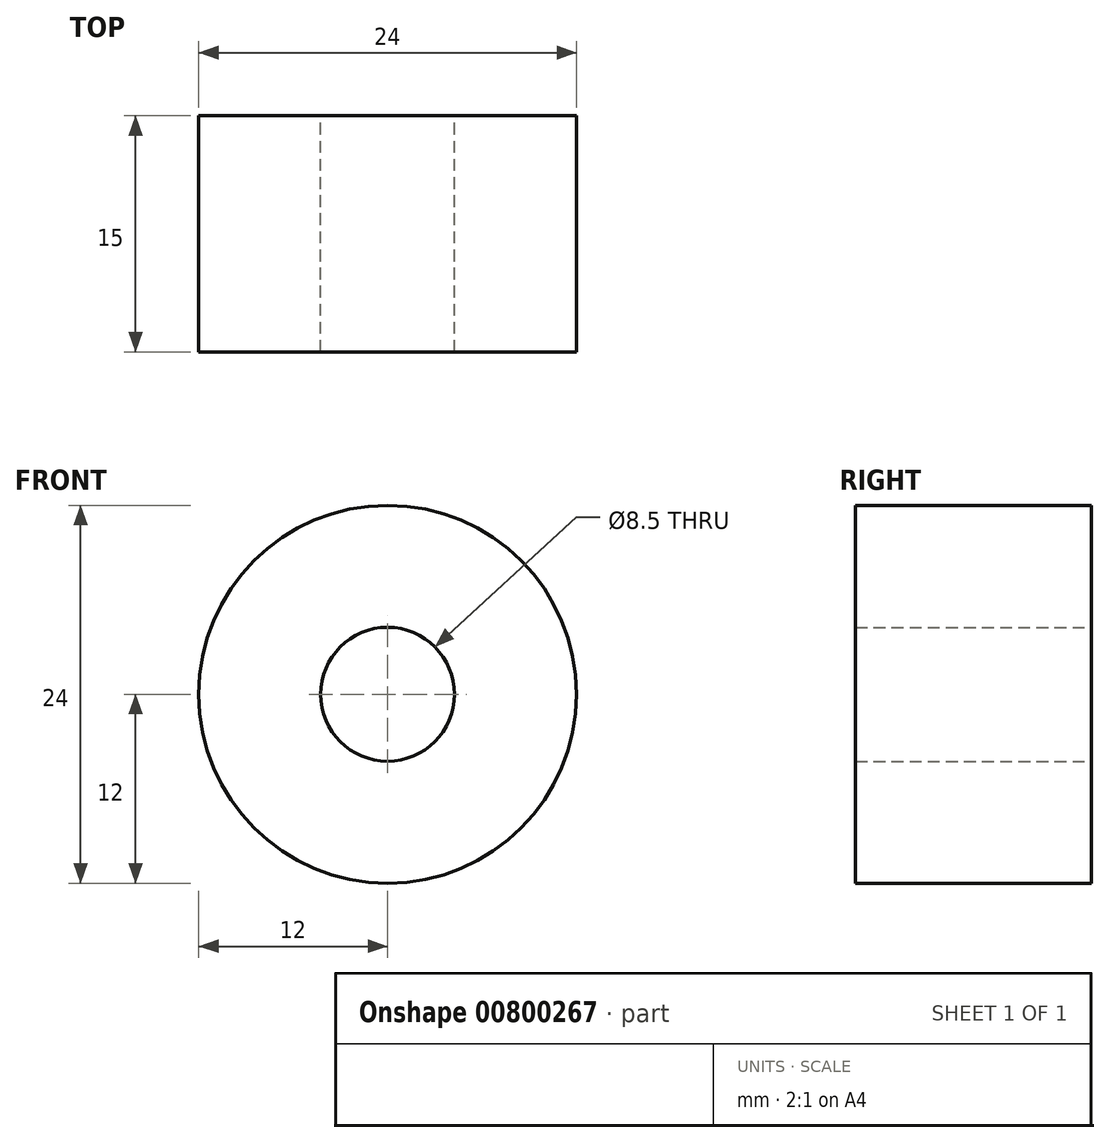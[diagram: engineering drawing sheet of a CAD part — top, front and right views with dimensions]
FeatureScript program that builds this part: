
annotation { "Feature Type Name" : "Feature", "Feature Type Description" : "" }
export const myFeature = defineFeature(function(context is Context, id is Id, definition is map)
    precondition{}
    {
        {
            var Q0;
            Q0=qCreatedBy(makeId("Front.planeOp"),FACE);
            var sketch = newSketch(context, id + "F0", { "sketchPlane" : qUnion([Q0])});
            skCircle(sketch, "E0", {"center": v(0, 0) * mm, "radius": 12 * mm});
            skCircle(sketch, "E1", {"center": v(0, 0) * mm, "radius": 4.25 * mm});
            skSolve(sketch);
        }
        {
            var Q0;
            Q0 = qSketchRegion(id + "F0", true);
            extrude(context, id + "F1", {"entities" : qUnion([Q0]), "depth" : 15 * mm, "offsetDistance" : 25 * mm});
        }
    });
